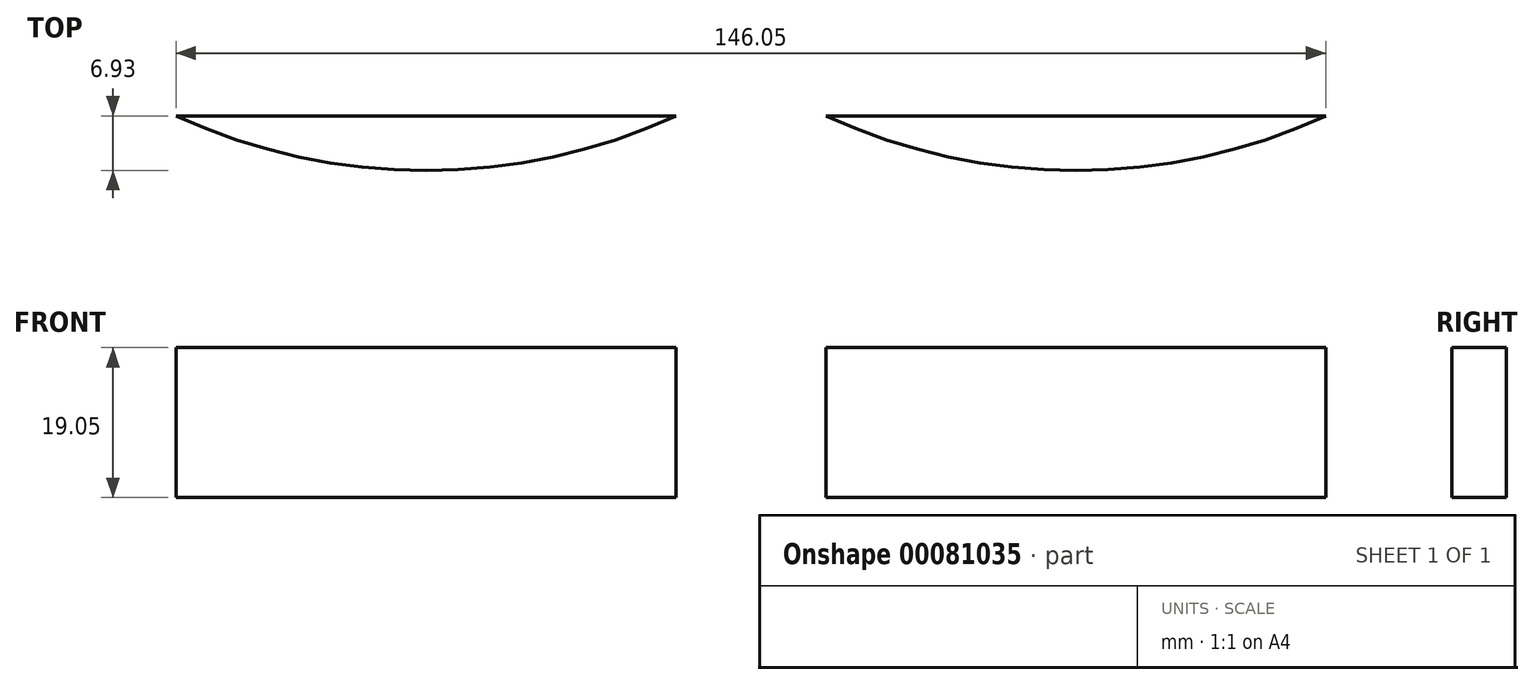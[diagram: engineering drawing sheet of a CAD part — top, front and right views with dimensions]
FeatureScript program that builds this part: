
annotation { "Feature Type Name" : "Feature", "Feature Type Description" : "" }
export const myFeature = defineFeature(function(context is Context, id is Id, definition is map)
    precondition{}
    {
        {
            var Q0;
            Q0=qCreatedBy(makeId("Front.planeOp"),FACE);
            var sketch = newSketch(context, id + "F0", { "sketchPlane" : qUnion([Q0])});
            skLineSegment(sketch, "E0.bottom", {"start": v(-129.2, -23.9) * mm, "end": v(124.8, -23.9) * mm});
            skLineSegment(sketch, "E0.top", {"start": v(-115.62, -42.95) * mm, "end": v(124.8, -42.95) * mm});
            skLineSegment(sketch, "E0.left", {"start": v(-129.2, -23.9) * mm, "end": v(-129.2, -29.37) * mm});
            skLineSegment(sketch, "E0.right", {"start": v(124.8, -23.9) * mm, "end": v(124.8, -42.95) * mm});
            skLineSegment(sketch, "E1", {"start": v(-129.2, -29.37) * mm, "end": v(-115.62, -42.95) * mm});
            skSolve(sketch);
        }
        {
            var Q0;
            Q0=makeQuery(id+"F0.imprint","IMPRINT",FACE,{"disambiguationData":[TD([[makeQuery(id+"F0.imprint","IMPRINT",EDGE,{"derivedFrom":sQuery(id+"F0.wireOp",EDGE,"E0.bottom")}),-1.0]])]});
            extrude(context, id + "F1", {"entities" : qUnion([Q0]), "depth" : 50.8 * mm});
        }
        {
            var Q0;
            Q0=qCreatedBy(makeId("Top.planeOp"),FACE);
            var sketch = newSketch(context, id + "F2", { "sketchPlane" : qUnion([Q0])});
            skCircle(sketch, "E2", {"center": v(-110.15, -25.4) * mm, "radius": 2.22 * mm});
            skCircle(sketch, "E3", {"center": v(-84.75, -25.4) * mm, "radius": 2.22 * mm});
            skSolve(sketch);
        }
        {
            var Q0;
            Q0=sQuery(id+"F2.wireOp",VERTEX,"E2.center");
            var Q1;
            Q1=sQuery(id+"F2.wireOp",VERTEX,"E3.center");
            var Q2;
            Q2=makeQuery(id+"F1.opExtrude","SWEPT_BODY",BODY,{"disambiguationData":[OSD([sQuery(id+"F0.wireOp",EDGE,"E0.bottom"),sQuery(id+"F0.wireOp",EDGE,"E0.top"),sQuery(id+"F0.wireOp",EDGE,"E0.left"),sQuery(id+"F0.wireOp",EDGE,"E0.right"),sQuery(id+"F0.wireOp",EDGE,"E1")])]});
            hole(context, id + "F3", {"style" : HoleStyle.SIMPLE, "endStyle" : HoleEndStyle.THROUGH, "holeDiameter" : 4.44 * mm, "locations" : qUnion([Q0, Q1]), "scope" : qUnion([Q2]), "isTappedThrough" : true});
        }
        {
            var Q0;
            Q0=makeQuery(id+"F1.opExtrude","SWEPT_FACE",FACE,{"disambiguationData":[OSD([sQuery(id+"F0.wireOp",EDGE,"E0.top")])]});
            var sketch = newSketch(context, id + "F4", { "sketchPlane" : qUnion([Q0])});
            skCircle(sketch, "E4", {"center": v(-110.15, 25.4) * mm, "radius": 4.76 * mm});
            skCircle(sketch, "E5", {"center": v(-84.75, 25.4) * mm, "radius": 4.76 * mm});
            skSolve(sketch);
        }
        {
            var Q0;
            Q0=sQuery(id+"F4.wireOp",VERTEX,"E4.center");
            var Q1;
            Q1=sQuery(id+"F4.wireOp",VERTEX,"E5.center");
            var Q2;
            Q2=makeQuery(id+"F1.opExtrude","SWEPT_BODY",BODY,{"disambiguationData":[OSD([sQuery(id+"F0.wireOp",EDGE,"E0.bottom"),sQuery(id+"F0.wireOp",EDGE,"E0.top"),sQuery(id+"F0.wireOp",EDGE,"E0.left"),sQuery(id+"F0.wireOp",EDGE,"E0.right"),sQuery(id+"F0.wireOp",EDGE,"E1")])]});
            hole(context, id + "F5", {"style" : HoleStyle.SIMPLE, "endStyle" : HoleEndStyle.BLIND, "holeDiameter" : 9.52 * mm, "holeDepth" : 5.08 * mm, "locations" : qUnion([Q0, Q1]), "scope" : qUnion([Q2])});
        }
        {
            var Q0;
            Q0=makeQuery(id+"F1.opExtrude","CAP_FACE",FACE,{"disambiguationData":[OSD([sQuery(id+"F0.wireOp",EDGE,"E0.bottom"),sQuery(id+"F0.wireOp",EDGE,"E0.top"),sQuery(id+"F0.wireOp",EDGE,"E0.left"),sQuery(id+"F0.wireOp",EDGE,"E0.right"),sQuery(id+"F0.wireOp",EDGE,"E1")])],"isStart":false});
            var sketch = newSketch(context, id + "F6", { "sketchPlane" : qUnion([Q0])});
            skText(sketch, "E6", { "text": "2\"", "fontName": "OpenSans-Regular.ttf"});
            const initialGuessF6  = {"E6": [0.074, -0.03586, 1, 0, 0.00488]};
            skSetInitialGuess(sketch, initialGuessF6);
            skSolve(sketch);
        }
        {
            var Q0;
            Q0 = qSketchRegion(id + "F6", true);
            extrude(context, id + "F7", {"entities" : qUnion([Q0]), "operationType" : NewBodyOperationType.REMOVE, "oppositeDirection" : true, "depth" : 2.54 * mm});
        }
        {
            var Q0;
            Q0=makeQuery(id+"F1.opExtrude","CAP_FACE",FACE,{"disambiguationData":[OSD([sQuery(id+"F0.wireOp",EDGE,"E0.bottom"),sQuery(id+"F0.wireOp",EDGE,"E0.top"),sQuery(id+"F0.wireOp",EDGE,"E0.left"),sQuery(id+"F0.wireOp",EDGE,"E0.right"),sQuery(id+"F0.wireOp",EDGE,"E1")])],"isStart":true});
            var sketch = newSketch(context, id + "F8", { "sketchPlane" : qUnion([Q0])});
            skText(sketch, "E7", { "text": "2\"\n", "fontName": "OpenSans-Regular.ttf"});
            const initialGuessF8  = {"E7": [-0.08015, -0.03586, 1, 0, 0.00488]};
            skSetInitialGuess(sketch, initialGuessF8);
            skSolve(sketch);
        }
        {
            var Q0;
            Q0 = qSketchRegion(id + "F8", true);
            extrude(context, id + "F9", {"entities" : qUnion([Q0]), "operationType" : NewBodyOperationType.REMOVE, "oppositeDirection" : true, "depth" : 2.54 * mm});
        }
        {
            var Q0;
            Q0=makeQuery(id+"F1.opExtrude","SWEPT_FACE",FACE,{"disambiguationData":[OSD([sQuery(id+"F0.wireOp",EDGE,"E0.bottom")])]});
            var sketch = newSketch(context, id + "F10", { "sketchPlane" : qUnion([Q0])});
            skArc(sketch, "E8", {"start": v(-46.65, -50.8) * mm, "mid": v(-78.4, -43.87) * mm, "end": v(-110.15, -50.8) * mm});
            skArc(sketch, "E9", {"start": v(35.9, -50.8) * mm, "mid": v(4.15, -43.87) * mm, "end": v(-27.6, -50.8) * mm});
            skLineSegment(sketch, "E10", {"start": v(-110.15, -50.8) * mm, "end": v(-46.65, -50.8) * mm});
            skLineSegment(sketch, "E11", {"start": v(-27.6, -50.8) * mm, "end": v(35.9, -50.8) * mm});
            skLineSegment(sketch, "E12", {"start": v(-129.2, -25.4) * mm, "end": v(124.8, -25.4) * mm, "construction": true});
            skArc(sketch, "E13.MirrorCS", {"start": v(-46.65, 0) * mm, "mid": v(-78.4, -6.93) * mm, "end": v(-110.15, 0) * mm});
            skArc(sketch, "E14.MirrorCS", {"start": v(35.9, 0) * mm, "mid": v(4.15, -6.93) * mm, "end": v(-27.6, 0) * mm});
            skSolve(sketch);
        }
        {
            var Q0;
            {var subQ0=sQuery(id+"F10.wireOp",EDGE,"E13.MirrorCS");Q0=makeQuery(id+"F10.imprint","IMPRINT",FACE,{"disambiguationData":[TD([[makeQuery(id+"F10.imprint","IMPRINT",EDGE,{"derivedFrom":subQ0}),-1.0]])]});}
            var Q1;
            {var subQ0=sQuery(id+"F10.wireOp",EDGE,"E14.MirrorCS");Q1=makeQuery(id+"F10.imprint","IMPRINT",FACE,{"disambiguationData":[TD([[makeQuery(id+"F10.imprint","IMPRINT",EDGE,{"derivedFrom":subQ0}),-1.0]])]});}
            var Q2;
            Q2=makeQuery(id+"F10.imprint","IMPRINT",FACE,{"disambiguationData":[TD([[makeQuery(id+"F10.imprint","IMPRINT",EDGE,{"derivedFrom":sQuery(id+"F10.wireOp",EDGE,"E9")}),1.0]])]});
            var Q3;
            Q3=makeQuery(id+"F10.imprint","IMPRINT",FACE,{"disambiguationData":[TD([[makeQuery(id+"F10.imprint","IMPRINT",EDGE,{"derivedFrom":sQuery(id+"F10.wireOp",EDGE,"E8")}),1.0]])]});
            extrude(context, id + "F11", {"entities" : qUnion([Q0, Q1, Q2, Q3]), "operationType" : NewBodyOperationType.REMOVE, "endBound" : BoundingType.THROUGH_ALL, "oppositeDirection" : true, "depth" : 25.4 * mm});
        }
    });
